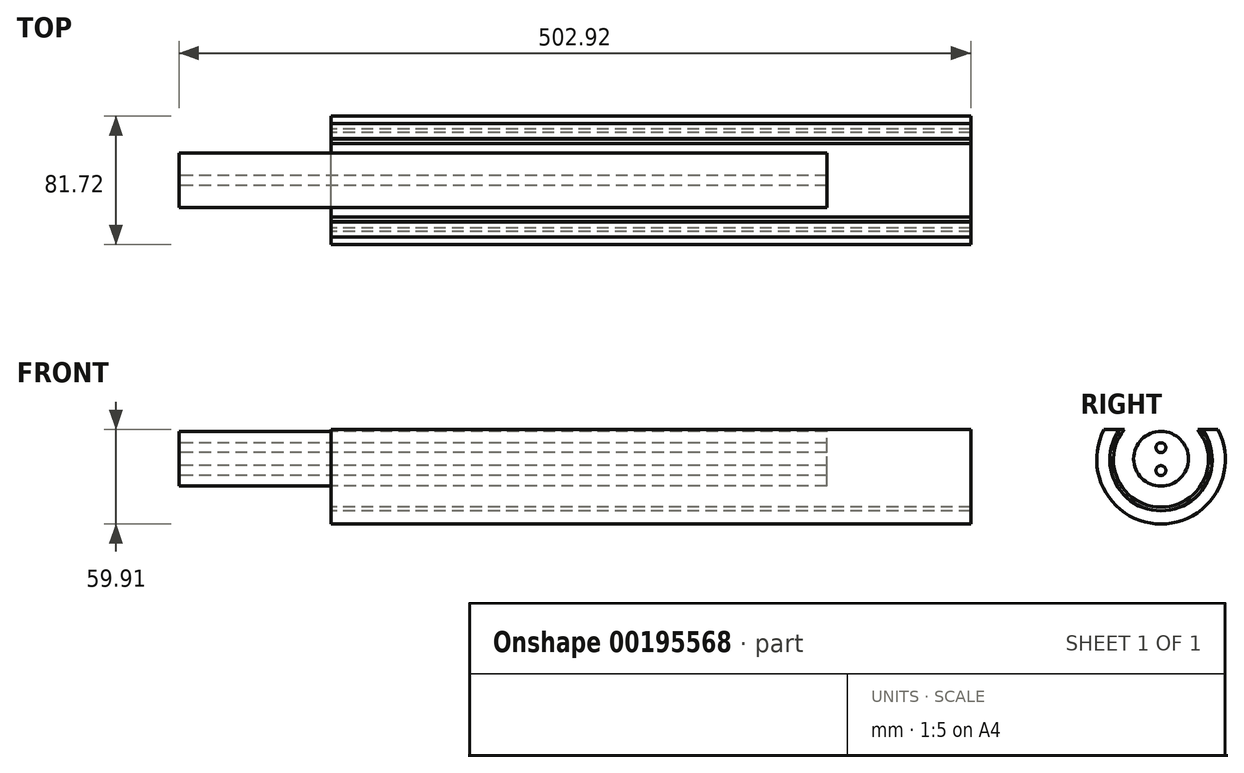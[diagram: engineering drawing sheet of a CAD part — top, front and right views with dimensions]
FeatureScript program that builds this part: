
annotation { "Feature Type Name" : "Feature", "Feature Type Description" : "" }
export const myFeature = defineFeature(function(context is Context, id is Id, definition is map)
    precondition{}
    {
        {
            var Q0;
            Q0=qCreatedBy(makeId("Right.planeOp"),FACE);
            var sketch = newSketch(context, id + "F0", { "sketchPlane" : qUnion([Q0])});
            skCircle(sketch, "E0", {"center": v(0, 0) * mm, "radius": 32.47 * mm});
            skCircle(sketch, "E1", {"center": v(0, 0) * mm, "radius": 30.17 * mm});
            skSolve(sketch);
        }
        {
            var Q0;
            Q0=qSketchRegion(id+"F0",true);
            extrude(context, id + "F1", {"entities" : qUnion([Q0]), "depth" : 203.2 * mm, "hasSecondDirection" : true, "secondDirectionOppositeDirection" : true, "secondDirectionDepth" : 203.2 * mm});
        }
        {
            var Q0;
            Q0=qCreatedBy(makeId("Right.planeOp"),FACE);
            var sketch = newSketch(context, id + "F2", { "sketchPlane" : qUnion([Q0])});
            skCircle(sketch, "E2", {"center": v(0, 0) * mm, "radius": 32.56 * mm});
            skCircle(sketch, "E3", {"center": v(0, 0) * mm, "radius": 40.86 * mm});
            skSolve(sketch);
        }
        {
            var Q0;
            Q0=qSketchRegion(id+"F2",true);
            extrude(context, id + "F3", {"entities" : qUnion([Q0]), "depth" : 203.2 * mm, "hasSecondDirection" : true, "secondDirectionOppositeDirection" : true, "secondDirectionDepth" : 203.2 * mm});
        }
        {
            var Q0;
            Q0=qCreatedBy(makeId("Right.planeOp"),FACE);
            var sketch = newSketch(context, id + "F4", { "sketchPlane" : qUnion([Q0])});
            skCircle(sketch, "E4", {"center": v(-0.08, 7.57) * mm, "radius": 3.15 * mm});
            skCircle(sketch, "E5", {"center": v(-0.08, -7) * mm, "radius": 3.15 * mm});
            skSolve(sketch);
        }
        {
            var Q0;
            Q0=qSketchRegion(id+"F4",true);
            extrude(context, id + "F5", {"entities" : qUnion([Q0]), "depth" : 111.76 * mm, "hasSecondDirection" : true, "secondDirectionOppositeDirection" : true, "secondDirectionDepth" : 299.72 * mm});
        }
        {
            var Q0;
            Q0=qCreatedBy(makeId("Top.planeOp"),FACE);
            cPlane(context, id + "F6", {"entities" : qUnion([Q0]), "cplaneType" : CPlaneType.OFFSET, "offset" : 19.05 * mm, "width" : 152.4 * mm, "height" : 152.4 * mm});
        }
        {
            var Q0;
            Q0=qCreatedBy(id+"F6.planeOp",FACE);
            var sketch = newSketch(context, id + "F7", { "sketchPlane" : qUnion([Q0])});
            skLineSegment(sketch, "E6.bottom", {"start": v(-214.92, 45.6) * mm, "end": v(211.11, 45.6) * mm});
            skLineSegment(sketch, "E6.top", {"start": v(-214.92, -47.34) * mm, "end": v(211.11, -47.34) * mm});
            skLineSegment(sketch, "E6.left", {"start": v(-214.92, 45.6) * mm, "end": v(-214.92, -47.34) * mm});
            skLineSegment(sketch, "E6.right", {"start": v(211.11, 45.6) * mm, "end": v(211.11, -47.34) * mm});
            skSolve(sketch);
        }
        {
            var Q0;
            Q0=qSketchRegion(id+"F7",true);
            extrude(context, id + "F8", {"entities" : qUnion([Q0]), "operationType" : NewBodyOperationType.REMOVE, "depth" : 35.81 * mm});
        }
        {
            var Q0;
            Q0=qCreatedBy(makeId("Right.planeOp"),FACE);
            var sketch = newSketch(context, id + "F9", { "sketchPlane" : qUnion([Q0])});
            skCircle(sketch, "E7", {"center": v(0, 0.5) * mm, "radius": 17.4 * mm});
            skSolve(sketch);
        }
        {
            var Q0;
            Q0 = qSketchRegion(id + "F9", true);
            extrude(context, id + "F10", {"entities" : qUnion([Q0]), "depth" : 111.76 * mm, "hasSecondDirection" : true, "secondDirectionOppositeDirection" : true, "secondDirectionDepth" : 299.72 * mm});
        }
    });
